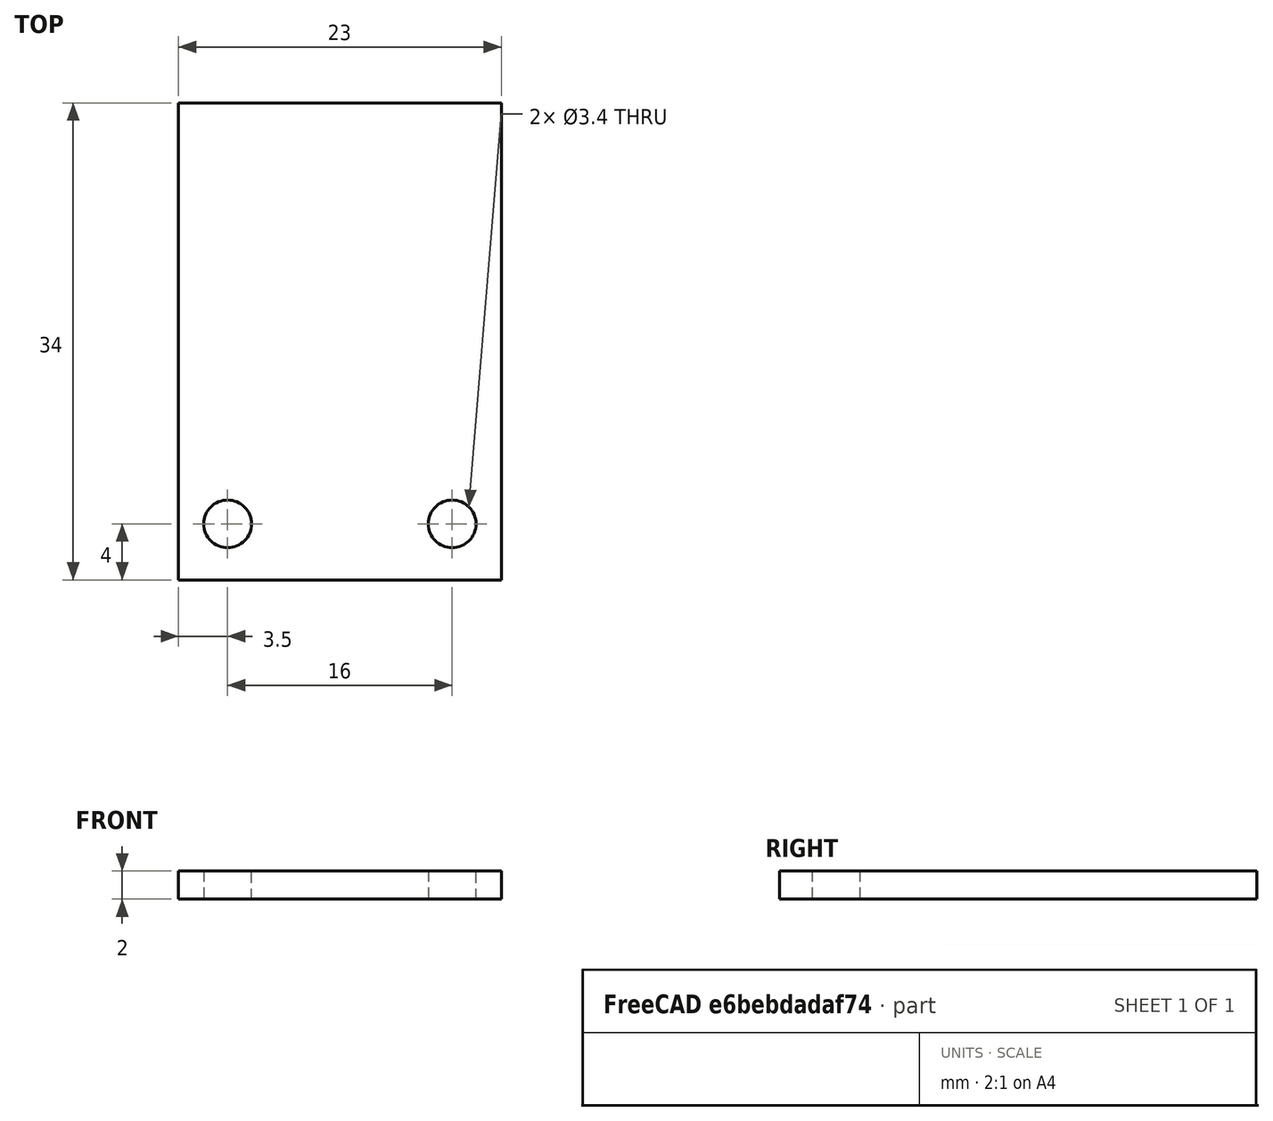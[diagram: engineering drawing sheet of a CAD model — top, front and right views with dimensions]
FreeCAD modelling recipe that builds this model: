
FCSTD DOCUMENT  (FreeCAD 0.18.4R)
Label: 9
License: All rights reserved
LicenseURL: http://en.wikipedia.org/wiki/All_rights_reserved
objects: Sketcher::SketchObject×1, PartDesign::Pad×1, PartDesign::Body×1
note: 4 computed .brp shape members not serialized (recipe doc carries the construction recipe); baked Part::Feature solids carry a one-line shape summary decoded from their .brp

FEATURE [Sketcher::SketchObject] Sketch  label="Unnamed"
  constraints (23):
    c: Coincident(g0,g1)
    c: Coincident(g1,g2)
    c: Coincident(g2,g3)
    c: Coincident(g3,g0)
    c: Horizontal(g0)
    c: Horizontal(g2)
    c: Vertical(g1)
    c: Vertical(g3)
    c: Coincident(g0,g-1)
    c: Distance(g2) = 23
    c: Distance(g1) = 34
    c: Distance(g4,g2) = 30
    c: Diameter(g4) = 3.4
    c: Equal(g5,g4)
    c: Distance(g5,g4) = 16
    c: Horizontal(g5,g4)
    c: Coincident(g6,g5)
    c: PointOnObject(g6,g3)
    c: Horizontal(g6)
    c: Coincident(g7,g4)
    c: PointOnObject(g7,g1)
    c: Horizontal(g7)
    c: Equal(g7,g6)
FEATURE [PartDesign::Pad] Pad  label="Unnamed"
  Length = 100
  Length2 = 100
  Type = 0
FEATURE [PartDesign::Body] Body
  Group = -> [Sketch,Pad]
  Origin = -> Origin
  Tip = -> Pad
